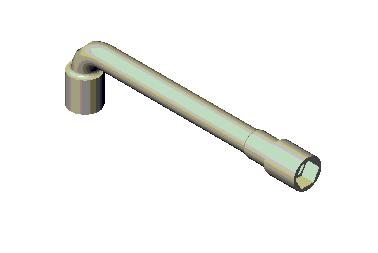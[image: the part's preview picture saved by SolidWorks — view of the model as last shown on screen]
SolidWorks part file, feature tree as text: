
SOLIDWORKS PART (.sldprt)
format: sldprt  version: not decoded by parser v0  size: 239,104 bytes
history: native  units: mm
features: sketch x15, plane x8, hole x4, extrude x3, fillet x3, cut_extrude x2, material x1, sweep x1 + 1 further entry (+8 scaffold rows collapsed)
feature tree (46):
  scaffold x8  (default folders/planes/origin — collapsed)
  material  "Matériau <non spécifié>"
  "Corps de surface"
  plane  "Plan1"
  plane  "Plan2"
  plane  "Plan3"
  sketch  "Esquisse1"  dims[D1=19.0mm]
  extrude  "Base-Extrusion"  Depth=20mm
  sketch  "Esquisse2"  dims[D1=15.0mm D2=15.0mm]
  extrude  "Boss.-Extru.1"  Depth=16mm
  sketch  "Esquisse3"  dims[D1=13.0mm]
  sketch  "Esquisse5"  dims[D2=14.0mm D1=100.0mm]
  sweep  "Boss.-Balayage1"
  fillet  "Congé5"  Radius=1mm
  fillet  "Congé6"  Radius=1mm
  sketch  "Esquisse6"  dims[D1=19.0mm]
  extrude  "Boss.-Extru.2"  Depth=20mm
  fillet  "Congé7"  Radius=2mm
  hole  "Perçage2"  Diameter=8mm Depth=43.5mm
  sketch  "Esquisse10"
  sketch  "Esquisse9"  dims[Diamètre=8.0mm Profondeur=43.5mm]
  sketch  "Esquisse11"  dims[c1.D1=8.0mm c1.D2=6.5mm c1.D3=6.5mm c2.D1=8.0mm c2.D2=6.5mm c2.D3=4.0mm c2.D4=6.5mm c2.D5=4.0mm c2.D6=~6.713703mm c3.D6=90.0deg c4.D6=8.0mm c4.D7=8.0mm c4.D1=8.0mm c5.D1=~251.318175deg c6.D1=8.0mm c7.D1=120.0deg c7.D2=8.0mm c8.D2=120.0deg c8.D3=8.0mm c9.D3=120.0deg c9.D4=~6.718379mm c10.D4=120.0deg c10.D5=~6.631704mm c11.D5=120.0deg c11.D6=8.0mm c11.D7=8.0mm c12.D6=6.93mm]
  cut_extrude  "Enlèv. mat.-Extru.2"  Depth=8mm
  hole  "Perçage3"  Diameter=12mm Depth=8mm
  sketch  "Esquisse13"
  sketch  "Esquisse12"  dims[c1.D1=~97.659253deg c1.D2=~82.982399deg c1.Diamètre=12.0mm c2.D2=100.0mm c2.D3=~82.982399deg c2.D4=90.0deg c3.D3=~97.716715deg c3.Profondeur=8.0mm c3.Angle=118.0deg]
  hole  "Perçage4"  Diameter=8mm Depth=32mm
  sketch  "Esquisse15"
  sketch  "Esquisse14"  dims[c1.D1=~97.659253deg c1.D2=~82.982399deg c1.Diamètre=8.0mm c2.D2=100.0mm c2.D3=~82.982399deg c2.D4=90.0deg c3.D3=~97.716715deg c3.Profondeur=32.0mm c3.Angle=118.0deg]
  sketch  "Esquisse16"  dims[c1.D1=~7.078068mm c2.D1=120.0deg c2.D2=~7.25494mm c3.D2=120.0deg c3.D3=8.0mm c4.D3=120.0deg c4.D4=~6.986947mm c5.D4=120.0deg c5.D5=8.0mm c6.D5=120.0deg c6.D1=~13.856406mm c7.D5=6.93mm]
  cut_extrude  "Enlèv. mat.-Extru.3"  Depth=8mm
  hole  "Perçage5"  Diameter=12mm Depth=10mm
  sketch  "Esquisse18"
  sketch  "Esquisse17"  dims[c1.D1=~97.659253deg c1.D2=~82.982399deg c1.Diamètre=12.0mm c2.D2=100.0mm c2.D3=~82.982399deg c2.D4=90.0deg c3.D3=~97.716715deg c3.Profondeur=10.0mm c3.Angle=118.0deg]
  plane  "Plan A"  Offset=5mm
  plane  "Plan B"  Offset=13mm
  plane  "Plan C"  Offset=13mm
  plane  "Plan D"  Offset=60mm
  plane  "Plan E"  Offset=64mm
decode coverage: 23 of 28 modeling features carry decoded parameters; 1 rows unclassified (native names shown)
note: ~ marks probable driven/reference dimensions
summary: Diameter pulled from absorbed wizard sketch
note: suppression state not decoded; provenance and decode notes live in map.json
